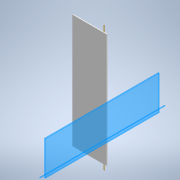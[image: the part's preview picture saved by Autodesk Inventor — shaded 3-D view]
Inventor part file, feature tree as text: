
AUTODESK INVENTOR PART (.ipt)
format: ipt  version: 2021 (Build 250183000, 183)  size: 97,280 bytes
history: native  units: mm
features: other x4, extrude x1, sketch x1, reference x1
ambient origin geometry x8: Origin, YZ Plane, XZ Plane, XY Plane, X Axis, Y Axis, Z Axis, Center Point
bodies: Body1 (feature_tree)
feature tree (7):
  other  "Bryła1"
  other  "Płaszczyzna konstrukcyjna1"
  extrude  "Wyciągnięcie proste1"  Depth=600.0mm
  sketch  "Szkic1"
  reference  "Odniesienie1"
  other  "Zespół1"
  other  "ISO 10799-2 - 25x25x2.5 - 2000:1"
